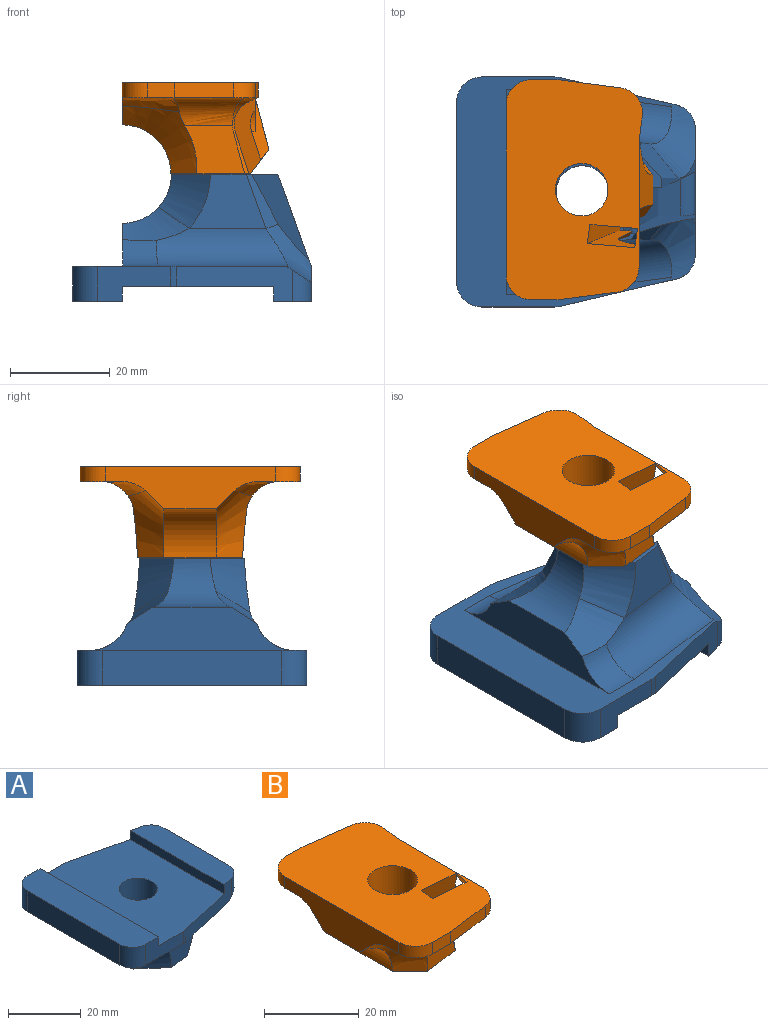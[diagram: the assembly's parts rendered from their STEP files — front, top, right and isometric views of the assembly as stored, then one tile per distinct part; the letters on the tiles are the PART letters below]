
ASSEMBLY  parts=2 mates=1
PART A: 43 faces, bbox 50.1x46.6x27.7 mm
  f0: plane 18.44x6.74mm, normal (0.94,0,-0.34), area 17.6mm2, adj f1,f2,f20,f21,f40
  f1: plane 21.38x21.03mm, normal (0,0,-1), area 190.7mm2, adj f0,f8,f10,f12,f20,f22,f25,f27
  f2: plane 25.65x7.43mm, normal (1,0,0), area 121.3mm2, adj f0,f7,f11,f21,f23,f28,f31,f40
  f3: plane 14.63x7mm, normal (0,1,0), area 73.4mm2, adj f14,f15,f29,f32,f36,f37
  f4: plane 14.63x7mm, normal (0,-1,0), area 73.4mm2, adj f14,f15,f30,f33,f36,f37
  f5: plane 23.23x7.09mm, normal (0.23,-0.97,0), area 105.8mm2, adj f7,f15,f21,f30,f31,f35,f37
  f6: plane 23.23x7.09mm, normal (0.23,0.97,0), area 105.8mm2, adj f7,f15,f23,f28,f29,f35,f37
  f7: plane 36.53x7.48mm, normal (0,0,1), area 253.9mm2, adj f2,f5,f6,f28,f31,f35
  f8: plane 15.4x10.84mm, normal (0.13,0.99,-0.05), area 114.8mm2, adj f1,f17,f22,f27
  f9: plane 41.65x9.3mm, normal (-1,0,0), area 229.2mm2, adj f12,f15,f16,f19,f24,f26
  f10: plane 15.4x10.84mm, normal (0.13,-0.99,-0.05), area 114.8mm2, adj f1,f18,f20,f25
  f11: plane 1.38x1.35mm, normal (0.94,0,-0.34), area 0.9mm2, adj f2,f23,f41
  f12: cylinder r=9.75mm len=15.62mm, axis (0,1,0), area 162.5mm2, adj f1,f9,f24,f25,f26,f27
  f13: plane 36x7mm, normal (-1,0,0), area 252mm2, adj f14,f15,f32,f33
  f14: plane 46x9.97mm, normal (0,0,1), area 448mm2, adj f3,f4,f13,f32,f33,f36
  f15: plane 46.02x42.92mm, normal (0,0,-1), area 580.6mm2, adj f3,f4,f5,f6,f9,f13,f16,f17
  f16: cylinder r=8mm len=7.57mm, axis (1,0,0), area 67.5mm2, adj f9,f15,f17,f26
  f17: cylinder r=8mm len=26.75mm, axis (0.99,-0.13,0), area 283.7mm2, adj f8,f15,f16,f23,f26
  f18: cylinder r=8mm len=26.75mm, axis (-0.99,-0.13,0), area 283.7mm2, adj f10,f15,f19,f21,f24
  f19: cylinder r=8mm len=7.57mm, axis (-1,0,0), area 67.5mm2, adj f9,f15,f18,f24
  f20: plane 10.82x9.53mm, normal (0.71,-0.65,-0.26), area 94.7mm2, adj f0,f1,f10,f21
  f21: bspline ~15.44x14.14mm, area 128.6mm2, adj f0,f2,f5,f15,f18,f20,f31
  f22: plane 10.82x6.36mm, normal (0.71,0.65,-0.26), area 30.9mm2, adj f1,f8,f23,f41
  f23: bspline ~15.44x14.14mm, area 101.5mm2, adj f2,f6,f11,f15,f17,f22,f28,f41
  f24: bspline ~13.72x9.36mm, area 90.8mm2, adj f9,f12,f18,f19,f25
  f25: bspline ~14.8x11.83mm, area 99mm2, adj f1,f10,f12,f24
  f26: bspline ~13.72x9.35mm, area 90.8mm2, adj f9,f12,f16,f17,f27
  f27: bspline ~14.8x11.83mm, area 99mm2, adj f1,f8,f12,f26
  f28: cylinder r=5mm len=6.28mm, axis (0,0,1), area 35.1mm2, adj f2,f6,f7,f23
  f29: cylinder r=5mm len=4mm, axis (0,0,1), area 4.6mm2, adj f3,f6,f15,f37
  f30: cylinder r=5mm len=4mm, axis (0,0,1), area 4.6mm2, adj f4,f5,f15,f37
  f31: cylinder r=5mm len=6.28mm, axis (0,0,-1), area 35.1mm2, adj f2,f5,f7,f21
  f32: cylinder r=5mm len=7mm, axis (0,0,-1), area 55mm2, adj f3,f13,f14,f15
  f33: cylinder r=5mm len=7mm, axis (0,0,1), area 55mm2, adj f4,f13,f14,f15
  f34: cylinder r=5.25mm len=22.4mm, axis (0,0,1), area 738.9mm2, adj f1,f37
  f35: plane 36.53x3mm, normal (-1,0,0), area 109.6mm2, adj f5,f6,f7,f37
  f36: plane 46x3mm, normal (1,0,0), area 138mm2, adj f3,f4,f14,f37
  f37: plane 46x30.3mm, normal (0,0,1), area 1212.2mm2, adj f3,f4,f5,f6,f29,f30,f34,f35
  f38: plane 20.03x12.4mm, normal (0.95,0.06,-0.32), area 185.8mm2, adj f1,f39,f40,f41
  f39: plane 8.86x4.48mm, normal (0,0.17,-0.98), area 40.3mm2, adj f38,f40,f41,f42
  f40: plane 21.42x13.85mm, normal (0,0.98,0.17), area 139.3mm2, adj f0,f1,f2,f38,f39,f42
  f41: plane 22.98x14.39mm, normal (0,-0.98,-0.17), area 102.7mm2, adj f1,f2,f11,f22,f23,f38,f39,f42
  f42: cylinder r=3mm len=9.38mm, axis (0,0.98,0.17), area 42.4mm2, adj f2,f39,f40,f41
PART B: 38 faces, bbox 34.2x45x19.2 mm
  f0: plane 5.8x3.47mm, normal (1,0,0), area 16mm2, adj f1,f17,f18,f23,f29,f34,f36
  f1: plane 20.59x10.8mm, normal (1,0,0), area 65.5mm2, adj f0,f2,f3,f8,f13,f17,f34,f37
  f2: plane 12.5x3.47mm, normal (0.73,-0.66,0.14), area 26mm2, adj f1,f3,f4,f8,f37
  f3: bspline ~13.77x13.39mm, area 2.3mm2, adj f1,f2,f37
  f4: plane 13.11x4.83mm, normal (0.79,0,-0.61), area 60.1mm2, adj f2,f8,f9,f21,f37
  f5: plane 12.17x9.78mm, normal (0.13,0.99,-0.05), area 86mm2, adj f9,f19,f21,f31,f32
  f6: plane 34.28x8.73mm, normal (-1,0,0), area 191.4mm2, adj f10,f11,f17,f18,f19,f20,f24,f26
  f7: plane 12.17x9.78mm, normal (0.13,-0.99,-0.05), area 86mm2, adj f9,f20,f22,f28,f29
  f8: plane 14.45x10.37mm, normal (0.97,0,0.26), area 87.1mm2, adj f1,f2,f4,f13,f21,f32
  f9: plane 21.04x15.93mm, normal (0,0,-1), area 194.7mm2, adj f4,f5,f7,f10,f19,f20,f21,f22
  f10: cylinder r=9.75mm len=10.59mm, axis (0,1,0), area 162.2mm2, adj f6,f9,f19,f20
  f11: plane 27.79x9.27mm, normal (0,0,-1), area 139.8mm2, adj f6,f13,f14,f15,f25,f26,f30,f31
  f12: plane 11.84x3mm, normal (0.13,-0.99,0), area 35.8mm2, adj f16,f17,f18,f23
  f13: plane 5.04x3.49mm, normal (0.99,-0.13,0), area 15.6mm2, adj f1,f8,f11,f17,f25,f32
  f14: plane 12.54x3mm, normal (0.13,0.99,0), area 37.9mm2, adj f11,f15,f17,f25
  f15: plane 5.4x3mm, normal (0,1,0), area 16.2mm2, adj f11,f14,f17,f26
  f16: plane 5.4x3mm, normal (0,-1,0), area 16.2mm2, adj f12,f17,f18,f24
  f17: plane 44x27.29mm, normal (0,0,1), area 999.4mm2, adj f0,f1,f6,f12,f13,f14,f15,f16
  f18: plane 27.1x9.27mm, normal (0,0,-1), area 135.7mm2, adj f0,f6,f12,f16,f23,f24,f27,f28
  f19: cone r=9.75mm half-angle=45deg, axis (0,1,0), area 146.7mm2, adj f5,f6,f9,f10,f30,f31
  f20: cone r=16.46mm half-angle=45deg, axis (0,-1,0), area 146.7mm2, adj f6,f7,f9,f10,f27,f28
  f21: plane 8.37x7.13mm, normal (0.73,0.66,0.14), area 59.6mm2, adj f4,f5,f8,f9,f32
  f22: plane 8.37x3.11mm, normal (0.73,-0.66,0.14), area 7.9mm2, adj f7,f9,f29,f36
  f23: cylinder r=5mm len=4.95mm, axis (0,0,1), area 21.6mm2, adj f0,f12,f17,f18
  f24: cylinder r=5mm len=5mm, axis (0,0,-1), area 23.6mm2, adj f6,f16,f17,f18
  f25: cylinder r=5mm len=5.6mm, axis (0,0,1), area 23.6mm2, adj f11,f13,f14,f17
  f26: cylinder r=5mm len=5mm, axis (0,0,1), area 23.6mm2, adj f6,f11,f15,f17
  f27: bspline ~13.24x8.71mm, area 63.2mm2, adj f6,f18,f20,f28
  f28: bspline ~17.25x8.08mm, area 109mm2, adj f7,f18,f20,f27,f29
  f29: bspline ~7.42x7.32mm, area 18mm2, adj f0,f7,f18,f22,f28,f36
  f30: bspline ~13.24x8.71mm, area 63.1mm2, adj f6,f11,f19,f31
  f31: bspline ~17.25x8.08mm, area 109mm2, adj f5,f11,f19,f30,f32
  f32: bspline ~14.06x13.65mm, area 67.2mm2, adj f5,f8,f11,f13,f21,f31
  f33: cylinder r=5.25mm len=18.2mm, axis (0,0,1), area 600.4mm2, adj f9,f17
  f34: plane 3.94x2.28mm, normal (-0.93,0.14,-0.33), area 6.3mm2, adj f0,f1,f17,f36,f37
  f35: plane 18.2x7.08mm, normal (0.94,-0.14,0.32), area 74.2mm2, adj f9,f17,f36,f37
  f36: plane 18.2x10.37mm, normal (0.08,0.98,0.17), area 86.6mm2, adj f0,f9,f17,f22,f29,f34,f35
  f37: plane 18.91x11.68mm, normal (-0.08,-0.98,-0.17), area 119.9mm2, adj f1,f2,f3,f4,f9,f17,f34,f35
PLACE A rot(axis=(-1,0,0),180deg) t=(0,0,-8.5)mm
PLACE B t=(-0.12,0.38,-8.32)mm
MATE parallel B.f9 <-> A.f1  axis (0,0,-1) through (-9.61,0.72,-8.32)mm
